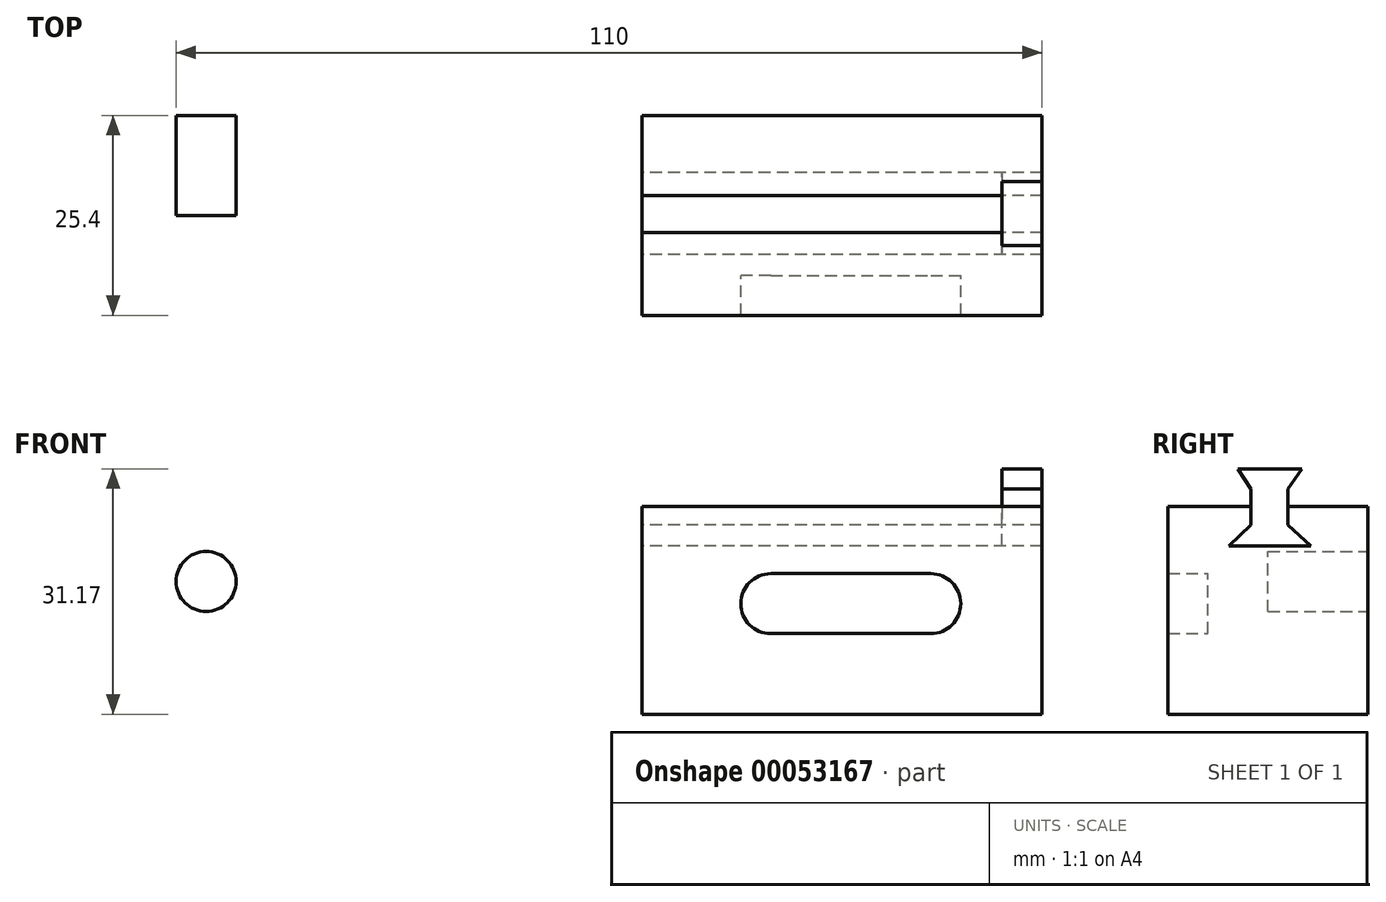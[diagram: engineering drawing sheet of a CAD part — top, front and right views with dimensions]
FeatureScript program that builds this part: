
annotation { "Feature Type Name" : "Feature", "Feature Type Description" : "" }
export const myFeature = defineFeature(function(context is Context, id is Id, definition is map)
    precondition{}
    {
        {
            var Q0;
            Q0=qCreatedBy(makeId("Right.planeOp"),FACE);
            var sketch = newSketch(context, id + "F0", { "sketchPlane" : qUnion([Q0])});
            skLineSegment(sketch, "E0.bottom", {"start": v(0, 0) * mm, "end": v(-25.4, 0) * mm});
            skLineSegment(sketch, "E0.top", {"start": v(0, 26.37) * mm, "end": v(-25.4, 26.37) * mm});
            skLineSegment(sketch, "E0.left", {"start": v(0, 0) * mm, "end": v(0, 26.37) * mm});
            skLineSegment(sketch, "E0.right", {"start": v(-25.4, 0) * mm, "end": v(-25.4, 26.37) * mm});
            skSolve(sketch);
        }
        {
            var Q0;
            Q0=makeQuery(id+"F0.imprint","IMPRINT",FACE,{"disambiguationData":[TD([[makeQuery(id+"F0.imprint","IMPRINT",EDGE,{"derivedFrom":sQuery(id+"F0.wireOp",EDGE,"E0.bottom")}),-1.0]])]});
            extrude(context, id + "F1", {"entities" : qUnion([Q0]), "depth" : 50.8 * mm});
        }
        {
            var Q0;
            Q0=qCreatedBy(makeId("Right.planeOp"),FACE);
            var sketch = newSketch(context, id + "F2", { "sketchPlane" : qUnion([Q0])});
            skLineSegment(sketch, "E1", {"start": v(-8.38, 31.17) * mm, "end": v(-10.16, 28.63) * mm});
            skLineSegment(sketch, "E2", {"start": v(-10.16, 28.63) * mm, "end": v(-10.16, 24.05) * mm});
            skLineSegment(sketch, "E3", {"start": v(-10.16, 24.05) * mm, "end": v(-7.24, 21.38) * mm});
            skLineSegment(sketch, "E4", {"start": v(-7.24, 21.38) * mm, "end": v(-17.66, 21.38) * mm});
            skLineSegment(sketch, "E5", {"start": v(-17.66, 21.38) * mm, "end": v(-14.87, 24.05) * mm});
            skLineSegment(sketch, "E6", {"start": v(-14.87, 24.05) * mm, "end": v(-14.87, 28.63) * mm});
            skLineSegment(sketch, "E7", {"start": v(-8.38, 31.17) * mm, "end": v(-16.52, 31.17) * mm});
            skLineSegment(sketch, "E8", {"start": v(-16.52, 31.17) * mm, "end": v(-14.87, 28.63) * mm});
            skSolve(sketch);
        }
        {
            var Q0;
            Q0=makeQuery(id+"F2.imprint","IMPRINT",FACE,{"disambiguationData":[TD([[makeQuery(id+"F2.imprint","IMPRINT",EDGE,{"derivedFrom":sQuery(id+"F2.wireOp",EDGE,"E1")}),-1.0]])]});
            extrude(context, id + "F3", {"entities" : qUnion([Q0]), "depth" : 50.8 * mm});
        }
        {
            var Q0;
            Q0=makeQuery(id+"F3.opExtrude","SWEPT_BODY",BODY,{"disambiguationData":[OSD([sQuery(id+"F2.wireOp",EDGE,"E1"),sQuery(id+"F2.wireOp",EDGE,"E2"),sQuery(id+"F2.wireOp",EDGE,"E3"),sQuery(id+"F2.wireOp",EDGE,"E4"),sQuery(id+"F2.wireOp",EDGE,"E5"),sQuery(id+"F2.wireOp",EDGE,"E6"),sQuery(id+"F2.wireOp",EDGE,"E7"),sQuery(id+"F2.wireOp",EDGE,"E8")])]});
            var Q1;
            Q1=makeQuery(id+"F1.opExtrude","SWEPT_BODY",BODY,{"disambiguationData":[OSD([sQuery(id+"F0.wireOp",EDGE,"E0.bottom"),sQuery(id+"F0.wireOp",EDGE,"E0.top"),sQuery(id+"F0.wireOp",EDGE,"E0.left"),sQuery(id+"F0.wireOp",EDGE,"E0.right")])]});
            booleanBodies(context, id + "F4", {"operationType" : BooleanOperationType.SUBTRACTION, "tools" : qUnion([Q0]), "targets" : qUnion([Q1]), "keepTools" : true});
        }
        {
            var Q0;
            Q0=makeQuery(id+"F3.opExtrude","CAP_FACE",FACE,{"disambiguationData":[OSD([sQuery(id+"F2.wireOp",EDGE,"E1"),sQuery(id+"F2.wireOp",EDGE,"E2"),sQuery(id+"F2.wireOp",EDGE,"E3"),sQuery(id+"F2.wireOp",EDGE,"E4"),sQuery(id+"F2.wireOp",EDGE,"E5"),sQuery(id+"F2.wireOp",EDGE,"E6"),sQuery(id+"F2.wireOp",EDGE,"E7"),sQuery(id+"F2.wireOp",EDGE,"E8")])],"isStart":true});
            extrude(context, id + "F5", {"entities" : qUnion([Q0]), "operationType" : NewBodyOperationType.REMOVE, "oppositeDirection" : true, "depth" : 45.72 * mm});
        }
        {
            var Q0;
            Q0=qCreatedBy(makeId("Front.planeOp"),FACE);
            var sketch = newSketch(context, id + "F6", { "sketchPlane" : qUnion([Q0])});
            skCircle(sketch, "E9", {"center": v(-55.4, 16.85) * mm, "radius": 3.81 * mm});
            skSolve(sketch);
        }
        {
            var Q0;
            Q0=makeQuery(id+"F6.imprint","IMPRINT",FACE,{"disambiguationData":[TD([[makeQuery(id+"F6.imprint","IMPRINT",EDGE,{"derivedFrom":sQuery(id+"F6.wireOp",EDGE,"E9")}),1.0]])]});
            extrude(context, id + "F7", {"entities" : qUnion([Q0]), "depth" : 12.7 * mm});
        }
        {
            var Q0;
            Q0=qCreatedBy(makeId("Front.planeOp"),FACE);
            var sketch = newSketch(context, id + "F8", { "sketchPlane" : qUnion([Q0])});
            skLineSegment(sketch, "E10.bottom", {"start": v(-56.82, 9.06) * mm, "end": v(-36.5, 9.06) * mm});
            skLineSegment(sketch, "E10.top", {"start": v(-56.82, 1.44) * mm, "end": v(-36.5, 1.44) * mm});
            skLineSegment(sketch, "E10.left", {"start": v(-56.82, 9.06) * mm, "end": v(-56.82, 1.44) * mm});
            skLineSegment(sketch, "E10.right", {"start": v(-36.5, 9.06) * mm, "end": v(-36.5, 1.44) * mm});
            skArc(sketch, "E11", {"start": v(-36.5, 1.44) * mm, "mid": v(-32.69, 5.25) * mm, "end": v(-36.5, 9.06) * mm});
            skArc(sketch, "E12", {"start": v(-56.82, 9.06) * mm, "mid": v(-60.63, 5.25) * mm, "end": v(-56.82, 1.44) * mm});
            skSolve(sketch);
        }
        {
            var Q0;
            Q0=makeQuery(id+"F8.imprint","IMPRINT",FACE,{"disambiguationData":[TD([[makeQuery(id+"F8.imprint","IMPRINT",EDGE,{"derivedFrom":sQuery(id+"F8.wireOp",EDGE,"E10.bottom")}),-1.0]])]});
            var Q1;
            Q1=makeQuery(id+"F8.imprint","IMPRINT",FACE,{"disambiguationData":[TD([[makeQuery(id+"F8.imprint","IMPRINT",EDGE,{"derivedFrom":sQuery(id+"F8.wireOp",EDGE,"E10.right")}),1.0]])]});
            var Q2;
            Q2=makeQuery(id+"F8.imprint","IMPRINT",FACE,{"disambiguationData":[TD([[makeQuery(id+"F8.imprint","IMPRINT",EDGE,{"derivedFrom":sQuery(id+"F8.wireOp",EDGE,"E10.left")}),-1.0]])]});
            extrude(context, id + "F9", {"entities" : qUnion([Q0, Q1, Q2]), "depth" : 5.08 * mm});
        }
        {
            var Q0;
            Q0=makeQuery(id+"F9.opExtrude","SWEPT_BODY",BODY,{"disambiguationData":[OSD([sQuery(id+"F8.wireOp",EDGE,"E10.bottom"),sQuery(id+"F8.wireOp",EDGE,"E10.top"),sQuery(id+"F8.wireOp",EDGE,"E11"),sQuery(id+"F8.wireOp",EDGE,"E12")])]});
            transform(context, id + "F10", {"entities" : qUnion([Q0]), "transformType" : TransformType.TRANSLATION_3D, "dx" : 73.15 * mm, "dy" : -20.32 * mm, "dz" : 8.8 * mm, "makeCopy" : false});
        }
        {
            var Q0;
            Q0=makeQuery(id+"F9.opExtrude","SWEPT_BODY",BODY,{"disambiguationData":[OSD([sQuery(id+"F8.wireOp",EDGE,"E10.bottom"),sQuery(id+"F8.wireOp",EDGE,"E10.top"),sQuery(id+"F8.wireOp",EDGE,"E11"),sQuery(id+"F8.wireOp",EDGE,"E12")])]});
            var Q1;
            Q1=makeQuery(id+"F1.opExtrude","SWEPT_BODY",BODY,{"disambiguationData":[OSD([sQuery(id+"F0.wireOp",EDGE,"E0.bottom"),sQuery(id+"F0.wireOp",EDGE,"E0.top"),sQuery(id+"F0.wireOp",EDGE,"E0.left"),sQuery(id+"F0.wireOp",EDGE,"E0.right")])]});
            booleanBodies(context, id + "F11", {"operationType" : BooleanOperationType.SUBTRACTION, "tools" : qUnion([Q0]), "targets" : qUnion([Q1])});
        }
    });
